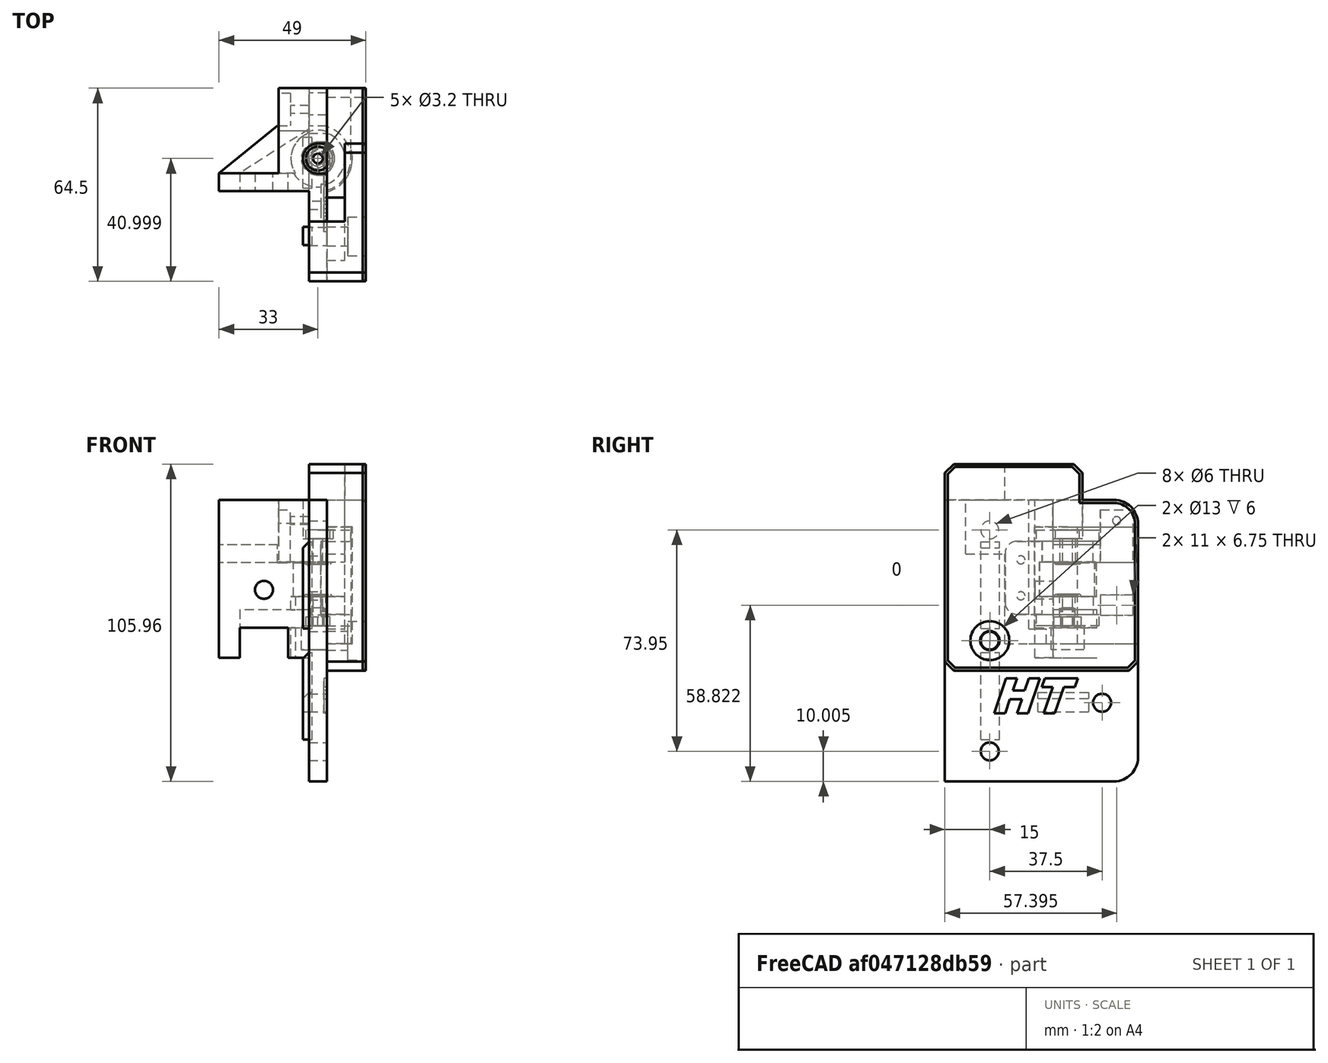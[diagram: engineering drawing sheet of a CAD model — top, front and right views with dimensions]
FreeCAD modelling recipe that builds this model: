
FCSTD DOCUMENT  (FreeCAD 0.18R16146 (Git))
Label: front-idler-right-2
License: All rights reserved
LicenseURL: http://en.wikipedia.org/wiki/All_rights_reserved
objects: Part::Cylinder×14, Part::Box×11, Part::MultiFuse×9, Part::Cut×8, Part::Chamfer×7, Part::Feature×5, Part::Fillet×1
note: 55 computed .brp shape members not serialized (recipe doc carries the construction recipe); baked Part::Feature solids carry a one-line shape summary decoded from their .brp

FEATURE [Part::Feature] Part__Feature  label="PulleyMount_FRONT_RIGHT_BodyV1.1"
  Placement = pos=(-440,-2.64,-417.58) rot=(1,0,0;1.5708rad)
  shape: bbox 44.04 x 64.54 x 93.99 mm, 115 faces (baked)
FEATURE [Part::Box] Box  label="Cube"
  AttacherType = Attacher::AttachEngine3D
  Height = 29
  Length = 3
  Placement = pos=(8,-8.1,14) rot=(0,0,1;0rad)
  Width = 6.2
FEATURE [Part::Box] Box001  label="Cube001"
  AttacherType = Attacher::AttachEngine3D
  Height = 29
  Length = 3
  Placement = pos=(8,-8.1,51) rot=(0,0,1;0rad)
  Width = 6.2
FEATURE [Part::Box] Box002  label="Cube002"
  AttacherType = Attacher::AttachEngine3D
  Height = 6.4
  Length = 3
  Placement = pos=(8,11,23.24) rot=(0,0,1;0rad)
  Width = 17
FEATURE [Part::Feature] Part__Feature001  label="PulleyMount_FRONT_RIGHT_BodyV1.002"
  shape: bbox 44.04 x 64.54 x 93.99 mm, 115 faces (baked)
FEATURE [Part::Cylinder] Cylinder  label="pos"
  Angle = 360
  AttacherType = Attacher::AttachEngine3D
  Height = 10
  Placement = pos=(13,20.8587,51.95) rot=(0,0,1;0rad)
  Radius = 1.6
FEATURE [Part::Cylinder] Cylinder001  label="pos001"
  Angle = 360
  AttacherType = Attacher::AttachEngine3D
  Height = 9.75
  Placement = pos=(13,20.8587,51.95) rot=(0,0,1;0rad)
  Radius = 5.55
FEATURE [Part::Cylinder] Cylinder002  label="pos002"
  Angle = 360
  AttacherType = Attacher::AttachEngine3D
  Height = 2
  Placement = pos=(13,20.8587,61.7) rot=(0,0,1;0rad)
  Radius = 6.55
FEATURE [Part::Cylinder] Cylinder003  label="pos003"
  Angle = 360
  AttacherType = Attacher::AttachEngine3D
  Height = 2
  Placement = pos=(13,20.8587,71.19) rot=(0,0,1;0rad)
  Radius = 6.55
FEATURE [Part::Cut] Cut
  Base = -> Part__Feature001
  Tool = -> Cylinder003
FEATURE [Part::Cut] Cut001
  Base = -> Cut
  Tool = -> Cylinder002
FEATURE [Part::Cylinder] Cylinder004  label="pos004"
  Angle = 360
  AttacherType = Attacher::AttachEngine3D
  Height = 10.75
  Placement = pos=(13,20.8587,73.2) rot=(0,0,1;0rad)
  Radius = 5.55
FEATURE [Part::MultiFuse] Fusion001
  Shapes = -> [Cut001,Cylinder004]
FEATURE [Part::Feature] Pad001
  Placement = pos=(13,20.86,51.95) rot=(0,0,1;0rad)
  shape: bbox 5.543 x 6.4 x 3 mm, 8 faces (baked)
FEATURE [Part::MultiFuse] Fusion002
  Shapes = -> [Fusion001,Cylinder001]
FEATURE [Part::Cut] Cut002
  Base = -> Fusion002
  Tool = -> Pad001
FEATURE [Part::Cylinder] Cylinder005  label="pos005"
  Angle = 360
  AttacherType = Attacher::AttachEngine3D
  Height = 35
  Placement = pos=(13,20.8587,51.95) rot=(0,0,1;0rad)
  Radius = 1.6
FEATURE [Part::Cut] Cut003
  Base = -> Cut002
  Tool = -> Cylinder005
FEATURE [Part::Cylinder] Cylinder006  label="pos006"
  Angle = 360
  AttacherType = Attacher::AttachEngine3D
  Height = 3
  Placement = pos=(13,20.8587,80.95) rot=(0,0,1;0rad)
  Radius = 4
FEATURE [Part::Cut] Cut004
  Base = -> Cut003
  Tool = -> Cylinder006
FEATURE [Part::Cylinder] Cylinder007  label="pos007"
  Angle = 360
  AttacherType = Attacher::AttachEngine3D
  Height = 0.75
  Placement = pos=(13,20.8587,129.95) rot=(0,0,1;0rad)
  Radius = 3.5
FEATURE [Part::Cylinder] Cylinder008  label="pos008"
  Angle = 360
  AttacherType = Attacher::AttachEngine3D
  Height = 0.75
  Placement = pos=(13,20.8587,129.95) rot=(0,0,1;0rad)
  Radius = 1.6
FEATURE [Part::Cut] Cut005
  Base = -> Cylinder007
  Placement = pos=(0,0,-68.25) rot=(0,0,1;0rad)
  Tool = -> Cylinder008
FEATURE [Part::Feature] Cut005001  label="Cut006"
  Placement = pos=(0,0,-57.51) rot=(0,0,1;0rad)
  shape: bbox 7 x 7 x 0.75 mm, 4 faces (baked)
FEATURE [Part::Chamfer] Chamfer003
  Base = -> Cut005001
  Edges = 1 edges r=0.5: [Edge3]
  Placement = pos=(0,0,0.1) rot=(0,0,1;0rad)
FEATURE [Part::Chamfer] Chamfer004
  Base = -> Cut005
  Edges = 1 edges r=0.5: [Edge1]
  Placement = pos=(0,0,-0.11) rot=(0,0,1;0rad)
FEATURE [Part::MultiFuse] Fusion003
  Shapes = -> [Chamfer004,Chamfer003,Cut004]
FEATURE [Part::Chamfer] Chamfer
  Base = -> Box001
  Edges = 1 edges r=2: [Edge2]
FEATURE [Part::Chamfer] Chamfer005
  Base = -> Box
  Edges = 1 edges r=2: [Edge2]
FEATURE [Part::Chamfer] Chamfer006
  Base = -> Box002
  Edges = 1 edges r=2: [Edge2]
FEATURE [Part::MultiFuse] Fusion
  Shapes = -> [Chamfer006,Chamfer005,Chamfer]
FEATURE [Part::Cylinder] Cylinder009  label="pos009"
  Angle = 360
  AttacherType = Attacher::AttachEngine3D
  Height = 6
  Placement = pos=(13,20.8587,51.95) rot=(0,0,1;0rad)
  Radius = 2.1
FEATURE [Part::Cylinder] Cylinder010  label="pos010"
  Angle = 360
  AttacherType = Attacher::AttachEngine3D
  Height = 6
  Placement = pos=(13,20.8587,51.95) rot=(0,0,1;0rad)
  Radius = 3.5
FEATURE [Part::MultiFuse] Fusion004
  Shapes = -> [Fusion003,Cylinder010]
FEATURE [Part::Cut] Cut005002
  Base = -> Fusion004
  Tool = -> Cylinder009
FEATURE [Part::Box] Box003  label="Cube003"
  AttacherType = Attacher::AttachEngine3D
  Height = 19
  Length = 3
  Placement = pos=(13,-7,17) rot=(0,0,1;0rad)
  Width = 33
FEATURE [Part::MultiFuse] Fusion005
  Shapes = -> [Box003,Cut005002]
FEATURE [Part::Box] Box004  label="Cube004"
  AttacherType = Attacher::AttachEngine3D
  Height = 12
  Length = 19
  Placement = pos=(10,-20.14,93.95) rot=(0,0,1;0rad)
  Width = 46
FEATURE [Part::Box] Box005  label="Cube005"
  AttacherType = Attacher::AttachEngine3D
  Height = 57
  Length = 13
  Placement = pos=(16,-20.14,36.95) rot=(0,0,1;0rad)
  Width = 64.5
FEATURE [Part::Cylinder] Cylinder011  label="pos011"
  Angle = 360
  AttacherType = Attacher::AttachEngine3D
  Height = 39
  Placement = pos=(13,20.8587,45.95) rot=(0,0,1;0rad)
  Radius = 11.5
FEATURE [Part::Box] Box006  label="Cube006"
  AttacherType = Attacher::AttachEngine3D
  Height = 48
  Length = 6
  Placement = pos=(16,-0.14,45.95) rot=(0,0,1;0rad)
  Width = 8
FEATURE [Part::Box] Box007  label="Cube007"
  AttacherType = Attacher::AttachEngine3D
  Height = 5
  Length = 6
  Placement = pos=(16,-0.14,45.95) rot=(0,0,1;0rad)
  Width = 42.5
FEATURE [Part::Box] Box008  label="Cube008"
  AttacherType = Attacher::AttachEngine3D
  Height = 39
  Length = 8
  Placement = pos=(16,20.86,45.95) rot=(0,0,1;0rad)
  Width = 26.5
FEATURE [Part::Box] Box009  label="Cube009"
  AttacherType = Attacher::AttachEngine3D
  Height = 18
  Length = 6
  Placement = pos=(16,-13.14,75.95) rot=(0,0,1;0rad)
  Width = 13
FEATURE [Part::Cylinder] Cylinder012  label="Cylinder"
  Angle = 360
  AttacherType = Attacher::AttachEngine3D
  Height = 30
  Placement = pos=(-1.04e-14,-5.1,47) rot=(0,1,0;1.5708rad)
  Radius = 3.2
FEATURE [Part::Cylinder] Cylinder013  label="Cylinder001"
  Angle = 360
  AttacherType = Attacher::AttachEngine3D
  Height = 7
  Placement = pos=(23,-5.1,47) rot=(0,1,0;1.5708rad)
  Radius = 6.5
FEATURE [Part::Fillet] Fillet
  Base = -> Box005
  Edges = 1 edges r=8: [Edge12]
FEATURE [Part::MultiFuse] Fusion006
  Shapes = -> [Cylinder013,Cylinder012]
FEATURE [Part::Box] Box010  label="Cube010"
  AttacherType = Attacher::AttachEngine3D
  Height = 12
  Length = 19
  Placement = pos=(3,-0.14,93.95) rot=(0,0,1;0rad)
  Width = 27
FEATURE [Part::MultiFuse] Fusion008
  Shapes = -> [Box004,Fillet]
FEATURE [Part::MultiFuse] Fusion009
  Shapes = -> [Box010,Fusion006,Box006,Box009,Cylinder011,Box007,Box008]
FEATURE [Part::Cut] Cut005003
  Base = -> Fusion008
  Tool = -> Fusion009
FEATURE [Part::Chamfer] Chamfer007
  Base = -> Cut005003
  Edges = 4 edges r=3: [Edge7,Edge9,Edge40,Edge82]
FEATURE [Part::Feature] Chamfer007001  label="Chamfer008"
  shape: bbox 19 x 64.5 x 69 mm, 30 faces (baked)
FEATURE [Part::Chamfer] Chamfer007002  label="wire-cover-big"
  Base = -> Chamfer007001
  Edges = 11 edges r=1: [Edge8,Edge12,Edge17,Edge18,Edge24,Edge43,Edge46,Edge52,Edge53,Edge59,Edge77]
